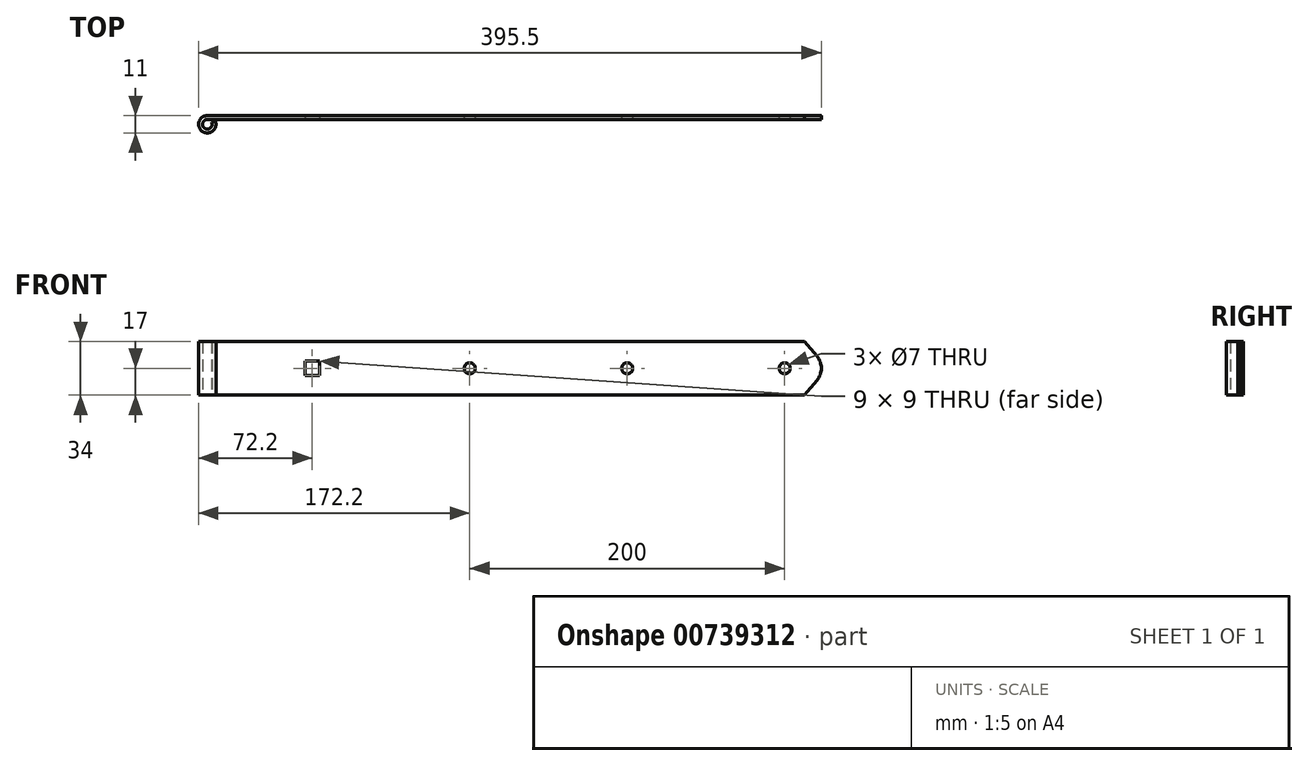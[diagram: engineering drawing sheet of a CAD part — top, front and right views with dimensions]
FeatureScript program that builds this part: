
annotation { "Feature Type Name" : "Feature", "Feature Type Description" : "" }
export const myFeature = defineFeature(function(context is Context, id is Id, definition is map)
    precondition{}
    {
        {
            var Q0;
            Q0=qCreatedBy(makeId("Top.planeOp"),FACE);
            var sketch = newSketch(context, id + "F0", { "sketchPlane" : qUnion([Q0])});
            skLineSegment(sketch, "E0", {"start": v(400, 5.5) * mm, "end": v(0, 5.5) * mm});
            skArc(sketch, "E1", {"start": v(0, 5.5) * mm, "mid": v(-3.1, -4.54) * mm, "end": v(5.12, 2) * mm});
            skArc(sketch, "E2.0", {"start": v(0, 3) * mm, "mid": v(-1.7, -2.48) * mm, "end": v(2.8, 1.1) * mm});
            skLineSegment(sketch, "E2.1", {"start": v(400, 3) * mm, "end": v(0, 3) * mm});
            skLineSegment(sketch, "E3", {"start": v(2.8, 1.1) * mm, "end": v(5.12, 2) * mm});
            skLineSegment(sketch, "E4", {"start": v(400, 5.5) * mm, "end": v(400, 3) * mm});
            skSolve(sketch);
        }
        {
            var Q0;
            Q0=makeQuery(id+"F0.imprint","IMPRINT",FACE,{"disambiguationData":[TD([[makeQuery(id+"F0.imprint","IMPRINT",EDGE,{"derivedFrom":sQuery(id+"F0.wireOp",EDGE,"E0")}),1.0]])]});
            extrude(context, id + "F1", {"entities" : qUnion([Q0]), "endBound" : BoundingType.SYMMETRIC, "depth" : 34 * mm, "offsetDistance" : 25 * mm});
        }
        {
            var Q0;
            Q0=makeQuery(id+"F1.opExtrude","SWEPT_FACE",FACE,{"disambiguationData":[OSD([sQuery(id+"F0.wireOp",EDGE,"E2.1")])]});
            var sketch = newSketch(context, id + "F2", { "sketchPlane" : qUnion([Q0])});
            skLineSegment(sketch, "E5", {"start": v(379.4, 17) * mm, "end": v(387.2, 7.71) * mm});
            skArc(sketch, "E6", {"start": v(387.2, -7.71) * mm, "mid": v(390, 0) * mm, "end": v(387.2, 7.71) * mm});
            skLineSegment(sketch, "E7", {"start": v(387.2, -7.71) * mm, "end": v(379.4, -17) * mm});
            skLineSegment(sketch, "E8.bottom", {"start": v(71.2, 4.5) * mm, "end": v(62.2, 4.5) * mm});
            skLineSegment(sketch, "E8.top", {"start": v(71.2, -4.5) * mm, "end": v(62.2, -4.5) * mm});
            skLineSegment(sketch, "E8.left", {"start": v(71.2, 4.5) * mm, "end": v(71.2, -4.5) * mm});
            skLineSegment(sketch, "E8.right", {"start": v(62.2, 4.5) * mm, "end": v(62.2, -4.5) * mm});
            skPoint(sketch, "E8.middle", {"position": v(66.7, 0) * mm});
            skCircle(sketch, "E9", {"center": v(166.7, 0) * mm, "radius": 3.5 * mm});
            skCircle(sketch, "E10.1.0.0", {"center": v(266.7, 0) * mm, "radius": 3.5 * mm});
            skCircle(sketch, "E10.2.0.0", {"center": v(366.7, 0) * mm, "radius": 3.5 * mm});
            skLineSegment(sketch, "E10.direction1", {"start": v(166.7, 0) * mm, "end": v(266.7, 0) * mm, "construction": true});
            skSolve(sketch);
        }
        {
            var Q0;
            {var subQ3=sQuery(id+"F2.wireOp",EDGE,"E5");Q0=makeQuery(id+"F2.imprint","IMPRINT",FACE,{"disambiguationData":[TD([[makeQuery(id+"F2.imprint","IMPRINT",EDGE,{"derivedFrom":subQ3}),1.0]])]});}
            var Q1;
            Q1=makeQuery(id+"F2.imprint","IMPRINT",FACE,{"disambiguationData":[TD([[makeQuery(id+"F2.imprint","IMPRINT",EDGE,{"derivedFrom":sQuery(id+"F2.wireOp",EDGE,"E8.bottom")}),1.0]])]});
            var Q2;
            Q2=makeQuery(id+"F2.imprint","IMPRINT",FACE,{"disambiguationData":[TD([[makeQuery(id+"F2.imprint","IMPRINT",EDGE,{"derivedFrom":sQuery(id+"F2.wireOp",EDGE,"E9")}),1.0]])]});
            var Q3;
            Q3=makeQuery(id+"F2.imprint","IMPRINT",FACE,{"disambiguationData":[TD([[makeQuery(id+"F2.imprint","IMPRINT",EDGE,{"derivedFrom":sQuery(id+"F2.wireOp",EDGE,"E10.1.0.0")}),1.0]])]});
            var Q4;
            Q4=makeQuery(id+"F2.imprint","IMPRINT",FACE,{"disambiguationData":[TD([[makeQuery(id+"F2.imprint","IMPRINT",EDGE,{"derivedFrom":sQuery(id+"F2.wireOp",EDGE,"E10.2.0.0")}),1.0]])]});
            extrude(context, id + "F3", {"entities" : qUnion([Q0, Q1, Q2, Q3, Q4]), "operationType" : NewBodyOperationType.REMOVE, "endBound" : BoundingType.UP_TO_NEXT, "oppositeDirection" : true, "depth" : 25 * mm, "offsetDistance" : 25 * mm});
        }
    });
